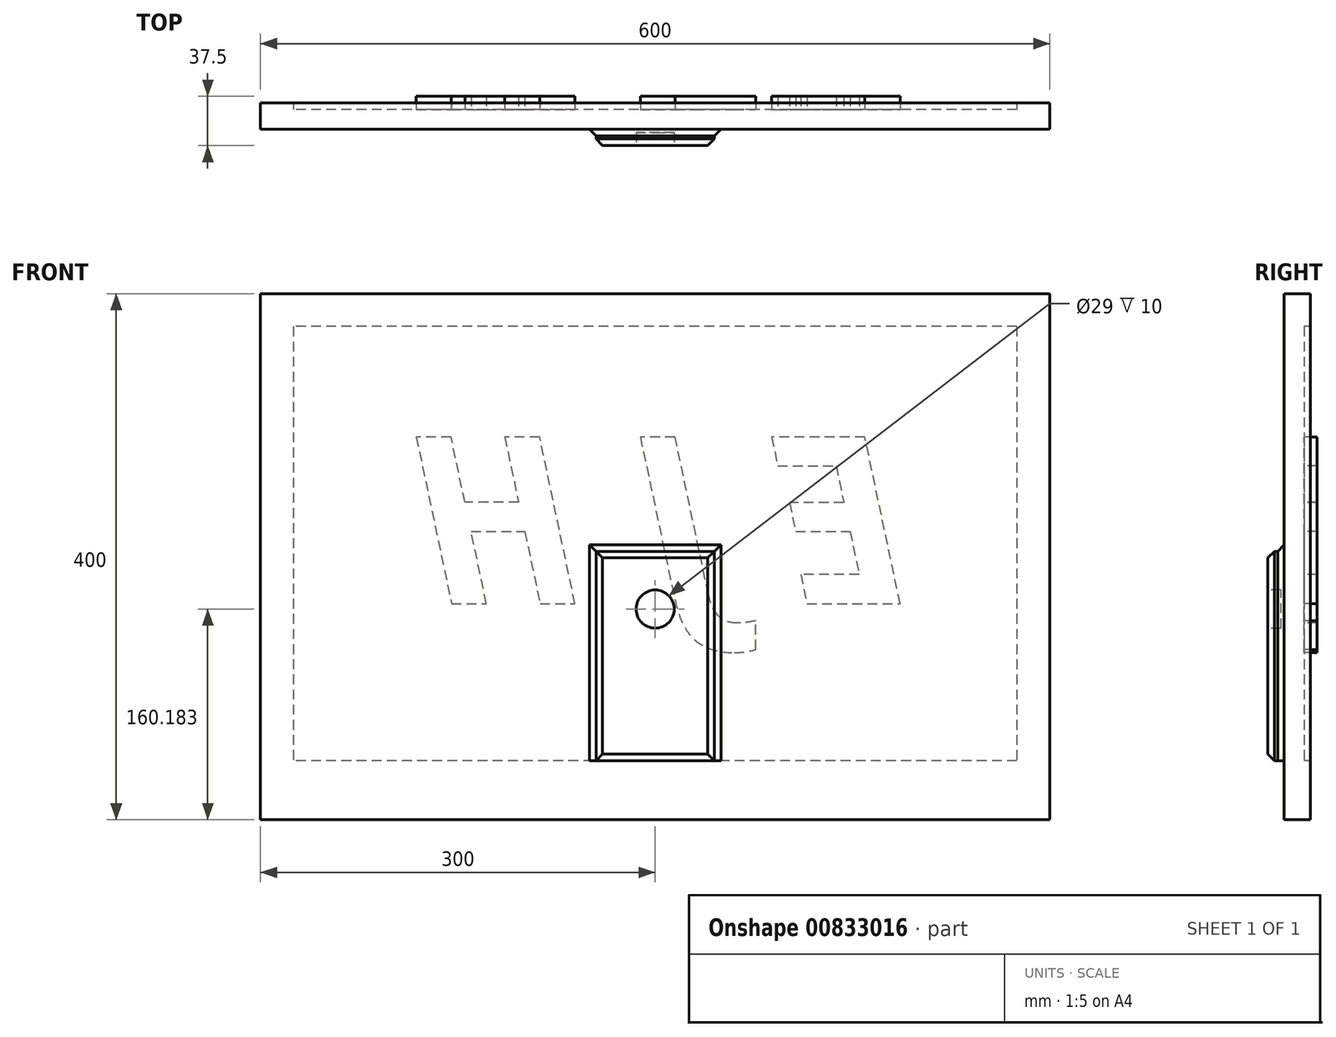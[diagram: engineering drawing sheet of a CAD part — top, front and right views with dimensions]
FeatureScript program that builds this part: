
annotation { "Feature Type Name" : "Feature", "Feature Type Description" : "" }
export const myFeature = defineFeature(function(context is Context, id is Id, definition is map)
    precondition{}
    {
        {
            var Q0;
            Q0=qCreatedBy(makeId("Front.planeOp"),FACE);
            var sketch = newSketch(context, id + "F0", { "sketchPlane" : qUnion([Q0])});
            skLineSegment(sketch, "E0.bottom", {"start": v(-300, 355) * mm, "end": v(300, 355) * mm});
            skLineSegment(sketch, "E0.top", {"start": v(-300, -45) * mm, "end": v(300, -45) * mm});
            skLineSegment(sketch, "E0.left", {"start": v(-300, 355) * mm, "end": v(-300, -45) * mm});
            skLineSegment(sketch, "E0.right", {"start": v(300, 355) * mm, "end": v(300, -45) * mm});
            skLineSegment(sketch, "E1.bottom", {"start": v(275, 330) * mm, "end": v(-275, 330) * mm});
            skLineSegment(sketch, "E1.top", {"start": v(275, 0) * mm, "end": v(-275, 0) * mm});
            skLineSegment(sketch, "E1.left", {"start": v(275, 330) * mm, "end": v(275, 0) * mm});
            skLineSegment(sketch, "E1.right", {"start": v(-275, 330) * mm, "end": v(-275, 0) * mm});
            skSolve(sketch);
        }
        {
            var Q0;
            Q0=makeQuery(id+"F0.imprint","IMPRINT",FACE,{"disambiguationData":[TD([[makeQuery(id+"F0.imprint","IMPRINT",EDGE,{"derivedFrom":sQuery(id+"F0.wireOp",EDGE,"E0.bottom")}),-1.0]])]});
            extrude(context, id + "F1", {"entities" : qUnion([Q0]), "oppositeDirection" : true, "depth" : 20 * mm, "offsetDistance" : 25 * mm});
        }
        {
            var Q0;
            Q0=makeQuery(id+"F0.imprint","IMPRINT",FACE,{"disambiguationData":[TD([[makeQuery(id+"F0.imprint","IMPRINT",EDGE,{"derivedFrom":sQuery(id+"F0.wireOp",EDGE,"E1.bottom")}),1.0]])]});
            var sketch = newSketch(context, id + "F2", { "sketchPlane" : qUnion([Q0])});
            skLineSegment(sketch, "E2.bottom", {"start": v(-45, 159.06) * mm, "end": v(45, 159.06) * mm});
            skLineSegment(sketch, "E2.top", {"start": v(-45, 0) * mm, "end": v(45, 0) * mm});
            skLineSegment(sketch, "E2.left", {"start": v(-45, 159.06) * mm, "end": v(-45, 0) * mm});
            skLineSegment(sketch, "E2.right", {"start": v(45, 159.06) * mm, "end": v(45, 0) * mm});
            skSolve(sketch);
        }
        {
            var Q0;
            Q0 = qSketchRegion(id + "F2", true);
            extrude(context, id + "F3", {"entities" : qUnion([Q0]), "operationType" : NewBodyOperationType.ADD, "endBound" : BoundingType.SYMMETRIC, "depth" : 25 * mm, "offsetDistance" : 25 * mm});
        }
        {
            var Q0;
            Q0=makeQuery(id+"F0.imprint","IMPRINT",FACE,{"disambiguationData":[TD([[makeQuery(id+"F0.imprint","IMPRINT",EDGE,{"derivedFrom":sQuery(id+"F0.wireOp",EDGE,"E1.bottom")}),1.0]])]});
            extrude(context, id + "F4", {"entities" : qUnion([Q0]), "operationType" : NewBodyOperationType.ADD, "oppositeDirection" : true, "depth" : 15 * mm, "offsetDistance" : 25 * mm});
        }
        {
            var Q0;
            Q0=makeQuery(id+"F3.opExtrude","CAP_FACE",FACE,{"disambiguationData":[OSD([sQuery(id+"F2.wireOp",EDGE,"E2.bottom"),sQuery(id+"F2.wireOp",EDGE,"E2.top"),sQuery(id+"F2.wireOp",EDGE,"E2.left"),sQuery(id+"F2.wireOp",EDGE,"E2.right")])],"isStart":false});
            var Q1;
            Q1=makeQuery(id+"F3.opExtrude","CAP_EDGE",EDGE,{"disambiguationData":[OSD([sQuery(id+"F2.wireOp",EDGE,"E2.right")])],"isStart":false});
            var Q2;
            Q2=makeQuery(id+"F4.boolean.opBoolean","INTERSECT",EDGE,{"derivedFrom":[makeQuery(id+"F3.opExtrude","SWEPT_FACE",FACE,{"disambiguationData":[OSD([sQuery(id+"F2.wireOp",EDGE,"E2.right")])]}),makeQuery(id+"F4.opExtrude","CAP_FACE",FACE,{"disambiguationData":[OSD([sQuery(id+"F0.wireOp",EDGE,"E1.bottom"),sQuery(id+"F0.wireOp",EDGE,"E1.top"),sQuery(id+"F0.wireOp",EDGE,"E1.left"),sQuery(id+"F0.wireOp",EDGE,"E1.right")])],"isStart":true})]});
            var Q3;
            Q3=makeQuery(id+"F4.boolean.opBoolean","INTERSECT",EDGE,{"derivedFrom":[makeQuery(id+"F3.opExtrude","SWEPT_FACE",FACE,{"disambiguationData":[OSD([sQuery(id+"F2.wireOp",EDGE,"E2.left")])]}),makeQuery(id+"F4.opExtrude","CAP_FACE",FACE,{"disambiguationData":[OSD([sQuery(id+"F0.wireOp",EDGE,"E1.bottom"),sQuery(id+"F0.wireOp",EDGE,"E1.top"),sQuery(id+"F0.wireOp",EDGE,"E1.left"),sQuery(id+"F0.wireOp",EDGE,"E1.right")])],"isStart":true})]});
            var Q4;
            Q4=makeQuery(id+"F4.boolean.opBoolean","INTERSECT",EDGE,{"derivedFrom":[makeQuery(id+"F3.opExtrude","SWEPT_FACE",FACE,{"disambiguationData":[OSD([sQuery(id+"F2.wireOp",EDGE,"E2.bottom")])]}),makeQuery(id+"F4.opExtrude","CAP_FACE",FACE,{"disambiguationData":[OSD([sQuery(id+"F0.wireOp",EDGE,"E1.bottom"),sQuery(id+"F0.wireOp",EDGE,"E1.top"),sQuery(id+"F0.wireOp",EDGE,"E1.left"),sQuery(id+"F0.wireOp",EDGE,"E1.right")])],"isStart":true})]});
            chamfer(context, id + "F5", {"entities" : qUnion([Q0, Q1, Q2, Q3, Q4]), "width" : 5 * mm, "tangentPropagation" : true});
        }
        {
            var Q0;
            Q0=makeQuery(id+"F3.opExtrude","CAP_FACE",FACE,{"disambiguationData":[OSD([sQuery(id+"F2.wireOp",EDGE,"E2.bottom"),sQuery(id+"F2.wireOp",EDGE,"E2.top"),sQuery(id+"F2.wireOp",EDGE,"E2.left"),sQuery(id+"F2.wireOp",EDGE,"E2.right")])],"isStart":false});
            var sketch = newSketch(context, id + "F6", { "sketchPlane" : qUnion([Q0])});
            skCircle(sketch, "E3", {"center": v(0, 115.18) * mm, "radius": 14.5 * mm});
            skSolve(sketch);
        }
        {
            var Q0;
            Q0=makeQuery(id+"F6.imprint","IMPRINT",FACE,{"disambiguationData":[TD([[makeQuery(id+"F6.imprint","IMPRINT",EDGE,{"derivedFrom":sQuery(id+"F6.wireOp",EDGE,"E3")}),1.0]])]});
            extrude(context, id + "F7", {"entities" : qUnion([Q0]), "operationType" : NewBodyOperationType.REMOVE, "oppositeDirection" : true, "depth" : 10 * mm, "offsetDistance" : 25 * mm});
        }
        {
            var Q0;
            Q0=makeQuery(id+"F4.opExtrude","CAP_FACE",FACE,{"disambiguationData":[OSD([sQuery(id+"F0.wireOp",EDGE,"E1.bottom"),sQuery(id+"F0.wireOp",EDGE,"E1.top"),sQuery(id+"F0.wireOp",EDGE,"E1.left"),sQuery(id+"F0.wireOp",EDGE,"E1.right")])],"isStart":false});
            var sketch = newSketch(context, id + "F8", { "sketchPlane" : qUnion([Q0])});
            skText(sketch, "E4", { "text": "E J H ", "fontName": "OpenSans-BoldItalic.ttf"});
            const initialGuessF8  = {"E4": [-0.19077, 0.11935, 1, 0, 0.1278]};
            skSetInitialGuess(sketch, initialGuessF8);
            skSolve(sketch);
        }
        {
            var Q0;
            Q0 = qSketchRegion(id + "F8", true);
            extrude(context, id + "F9", {"entities" : qUnion([Q0]), "operationType" : NewBodyOperationType.ADD, "depth" : 10 * mm, "offsetDistance" : 25 * mm});
        }
    });
